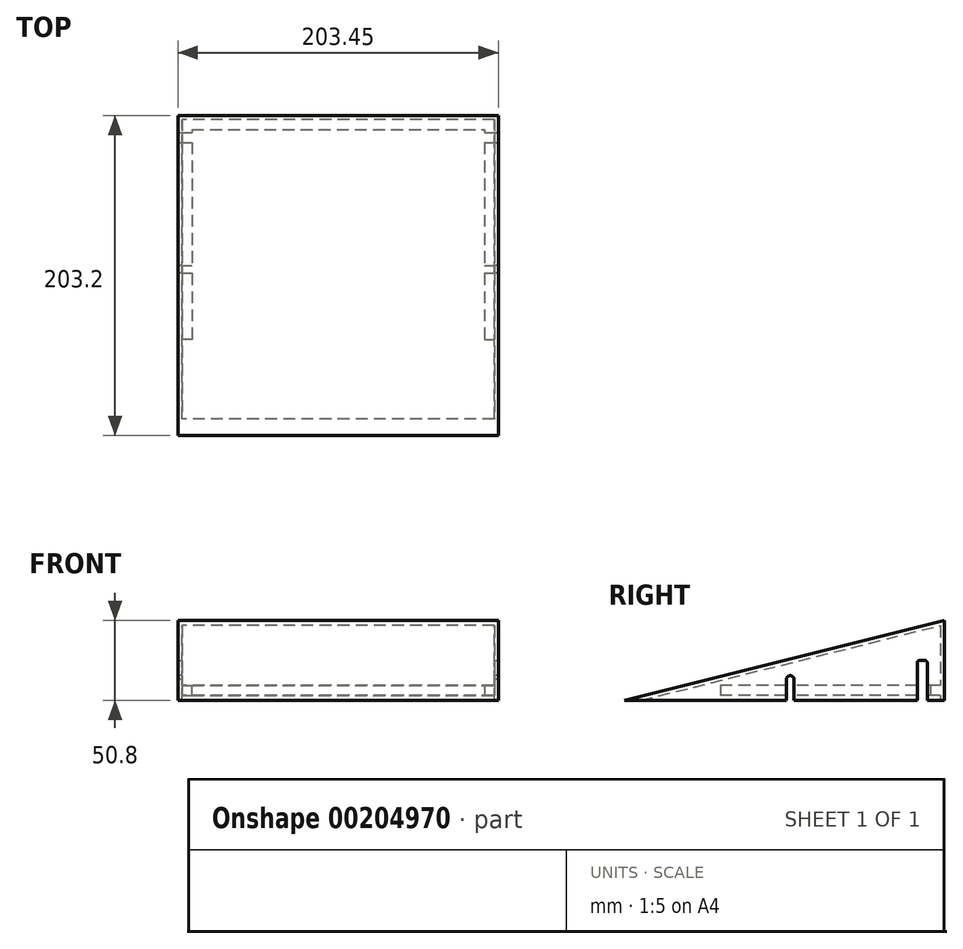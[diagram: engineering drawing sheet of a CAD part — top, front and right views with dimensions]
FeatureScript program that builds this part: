
annotation { "Feature Type Name" : "Feature", "Feature Type Description" : "" }
export const myFeature = defineFeature(function(context is Context, id is Id, definition is map)
    precondition{}
    {
        {
            var Q0;
            Q0=qCreatedBy(makeId("Right.planeOp"),FACE);
            var sketch = newSketch(context, id + "F0", { "sketchPlane" : qUnion([Q0])});
            skLineSegment(sketch, "E0", {"start": v(95.28, 0) * mm, "end": v(-107.92, 0) * mm});
            skLineSegment(sketch, "E1", {"start": v(-107.92, 0) * mm, "end": v(95.28, 50.8) * mm});
            skLineSegment(sketch, "E2", {"start": v(95.28, 50.8) * mm, "end": v(95.28, 0) * mm});
            skSolve(sketch);
        }
        {
            var Q0;
            Q0 = qSketchRegion(id + "F0", true);
            extrude(context, id + "F1", {"entities" : qUnion([Q0]), "depth" : 203.45 * mm});
        }
        {
            var Q0;
            Q0=makeQuery(id+"F1.opExtrude","SWEPT_FACE",FACE,{"disambiguationData":[OSD([sQuery(id+"F0.wireOp",EDGE,"E0")])]});
            shell(context, id + "F2", {"entities" : qUnion([Q0]), "thickness" : 2.54 * mm});
        }
        {
            var Q0;
            {var subQ0=sQuery(id+"F0.wireOp",EDGE,"E2");var subQ1=sQuery(id+"F0.wireOp",EDGE,"E1");var subQ2=sQuery(id+"F0.wireOp",EDGE,"E0");Q0=makeQuery(id+"F2.opShell","OFFSET_FACE",FACE,{"disambiguationData":[OSD([subQ2,subQ1,subQ0]),TDD([makeQuery(id+"F1.opExtrude","CAP_FACE",FACE,{"disambiguationData":[OSD([subQ2,subQ1,subQ0])],"isStart":true})])]});}
            var sketch = newSketch(context, id + "F3", { "sketchPlane" : qUnion([Q0])});
            skLineSegment(sketch, "E3.bottom", {"start": v(92.74, 9.53) * mm, "end": v(-46.96, 9.53) * mm});
            skLineSegment(sketch, "E3.top", {"start": v(92.74, 3.18) * mm, "end": v(-46.96, 3.18) * mm});
            skLineSegment(sketch, "E3.left", {"start": v(92.74, 9.53) * mm, "end": v(92.74, 3.18) * mm});
            skLineSegment(sketch, "E3.right", {"start": v(-46.96, 9.53) * mm, "end": v(-46.96, 3.18) * mm});
            skSolve(sketch);
        }
        {
            var Q0;
            Q0 = qSketchRegion(id + "F3", true);
            extrude(context, id + "F4", {"entities" : qUnion([Q0]), "operationType" : NewBodyOperationType.ADD, "depth" : 6.35 * mm});
        }
        {
            var Q0;
            {var subQ0=sQuery(id+"F0.wireOp",EDGE,"E2");var subQ1=sQuery(id+"F0.wireOp",EDGE,"E1");var subQ2=sQuery(id+"F0.wireOp",EDGE,"E0");Q0=makeQuery(id+"F2.opShell","OFFSET_FACE",FACE,{"disambiguationData":[OSD([subQ2,subQ1,subQ0]),TDD([makeQuery(id+"F1.opExtrude","CAP_FACE",FACE,{"disambiguationData":[OSD([subQ2,subQ1,subQ0])],"isStart":false})])]});}
            var sketch = newSketch(context, id + "F5", { "sketchPlane" : qUnion([Q0])});
            skLineSegment(sketch, "E4.bottom", {"start": v(-92.74, 9.52) * mm, "end": v(46.96, 9.52) * mm});
            skLineSegment(sketch, "E4.top", {"start": v(-92.74, 3.18) * mm, "end": v(46.96, 3.18) * mm});
            skLineSegment(sketch, "E4.left", {"start": v(-92.74, 9.52) * mm, "end": v(-92.74, 3.18) * mm});
            skLineSegment(sketch, "E4.right", {"start": v(46.96, 9.52) * mm, "end": v(46.96, 3.18) * mm});
            skSolve(sketch);
        }
        {
            var Q0;
            Q0 = qSketchRegion(id + "F5", true);
            extrude(context, id + "F6", {"entities" : qUnion([Q0]), "operationType" : NewBodyOperationType.ADD, "depth" : 6.35 * mm});
        }
        {
            var Q0;
            Q0=makeQuery(id+"F2.opShell","OFFSET_FACE",FACE,{"disambiguationData":[OSD([sQuery(id+"F0.wireOp",EDGE,"E2")])]});
            var sketch = newSketch(context, id + "F7", { "sketchPlane" : qUnion([Q0])});
            skLineSegment(sketch, "E5.bottom", {"start": v(8.89, 3.18) * mm, "end": v(194.56, 3.18) * mm});
            skLineSegment(sketch, "E5.top", {"start": v(8.89, 9.52) * mm, "end": v(194.56, 9.52) * mm});
            skLineSegment(sketch, "E5.left", {"start": v(8.89, 3.18) * mm, "end": v(8.89, 9.52) * mm});
            skLineSegment(sketch, "E5.right", {"start": v(194.56, 3.18) * mm, "end": v(194.56, 9.52) * mm});
            skSolve(sketch);
        }
        {
            var Q0;
            Q0 = qSketchRegion(id + "F7", true);
            extrude(context, id + "F8", {"entities" : qUnion([Q0]), "operationType" : NewBodyOperationType.ADD, "depth" : 6.35 * mm});
        }
        {
            var Q0;
            Q0=makeQuery(id+"F1.opExtrude","CAP_FACE",FACE,{"disambiguationData":[OSD([sQuery(id+"F0.wireOp",EDGE,"E0"),sQuery(id+"F0.wireOp",EDGE,"E1"),sQuery(id+"F0.wireOp",EDGE,"E2")])],"isStart":false});
            var sketch = newSketch(context, id + "F9", { "sketchPlane" : qUnion([Q0])});
            skLineSegment(sketch, "E6.bottom", {"start": v(84.49, 0) * mm, "end": v(78.14, 0) * mm});
            skLineSegment(sketch, "E6.top", {"start": v(82.9, 25.4) * mm, "end": v(79.72, 25.4) * mm});
            skLineSegment(sketch, "E6.left", {"start": v(84.49, 0) * mm, "end": v(84.49, 23.81) * mm});
            skLineSegment(sketch, "E6.right", {"start": v(78.14, 0) * mm, "end": v(78.14, 23.81) * mm});
            skPoint(sketch, "E6.middle", {"position": v(81.31, 12.7) * mm});
            skPoint(sketch, "E7.visualSharp", {"position": v(84.49, 25.4) * mm});
            skArc(sketch, "E7.filletArc", {"start": v(84.49, 23.81) * mm, "mid": v(84.02, 24.94) * mm, "end": v(82.9, 25.4) * mm});
            skPoint(sketch, "E8.visualSharp", {"position": v(78.14, 25.4) * mm});
            skArc(sketch, "E8.filletArc", {"start": v(79.72, 25.4) * mm, "mid": v(78.6, 24.94) * mm, "end": v(78.14, 23.81) * mm});
            skSolve(sketch);
        }
        {
            var Q0;
            Q0 = qSketchRegion(id + "F9", true);
            extrude(context, id + "F10", {"entities" : qUnion([Q0]), "operationType" : NewBodyOperationType.REMOVE, "endBound" : BoundingType.THROUGH_ALL, "oppositeDirection" : true, "depth" : 25.4 * mm});
        }
        {
            var Q0;
            Q0=makeQuery(id+"F1.opExtrude","CAP_FACE",FACE,{"disambiguationData":[OSD([sQuery(id+"F0.wireOp",EDGE,"E0"),sQuery(id+"F0.wireOp",EDGE,"E1"),sQuery(id+"F0.wireOp",EDGE,"E2")])],"isStart":true});
            var sketch = newSketch(context, id + "F11", { "sketchPlane" : qUnion([Q0])});
            skCircle(sketch, "E9", {"center": v(2.5, 13.34) * mm, "radius": 2.38 * mm});
            skLineSegment(sketch, "E10", {"start": v(0.13, 13.31) * mm, "end": v(0.13, 0) * mm});
            skLineSegment(sketch, "E11", {"start": v(4.9, 13.34) * mm, "end": v(4.9, 0) * mm});
            skSolve(sketch);
        }
        {
            var Q0;
            Q0 = qSketchRegion(id + "F11", true);
            var Q1;
            {var subQ0=sQuery(id+"F11.wireOp",EDGE,"E10");Q1=makeQuery(id+"F11.imprint","IMPRINT",FACE,{"disambiguationData":[TD([[makeQuery(id+"F11.imprint","IMPRINT",EDGE,{"derivedFrom":subQ0}),1.0]])]});}
            extrude(context, id + "F12", {"entities" : qUnion([Q0, Q1]), "operationType" : NewBodyOperationType.REMOVE, "endBound" : BoundingType.THROUGH_ALL, "oppositeDirection" : true, "depth" : 25.4 * mm});
        }
    });
